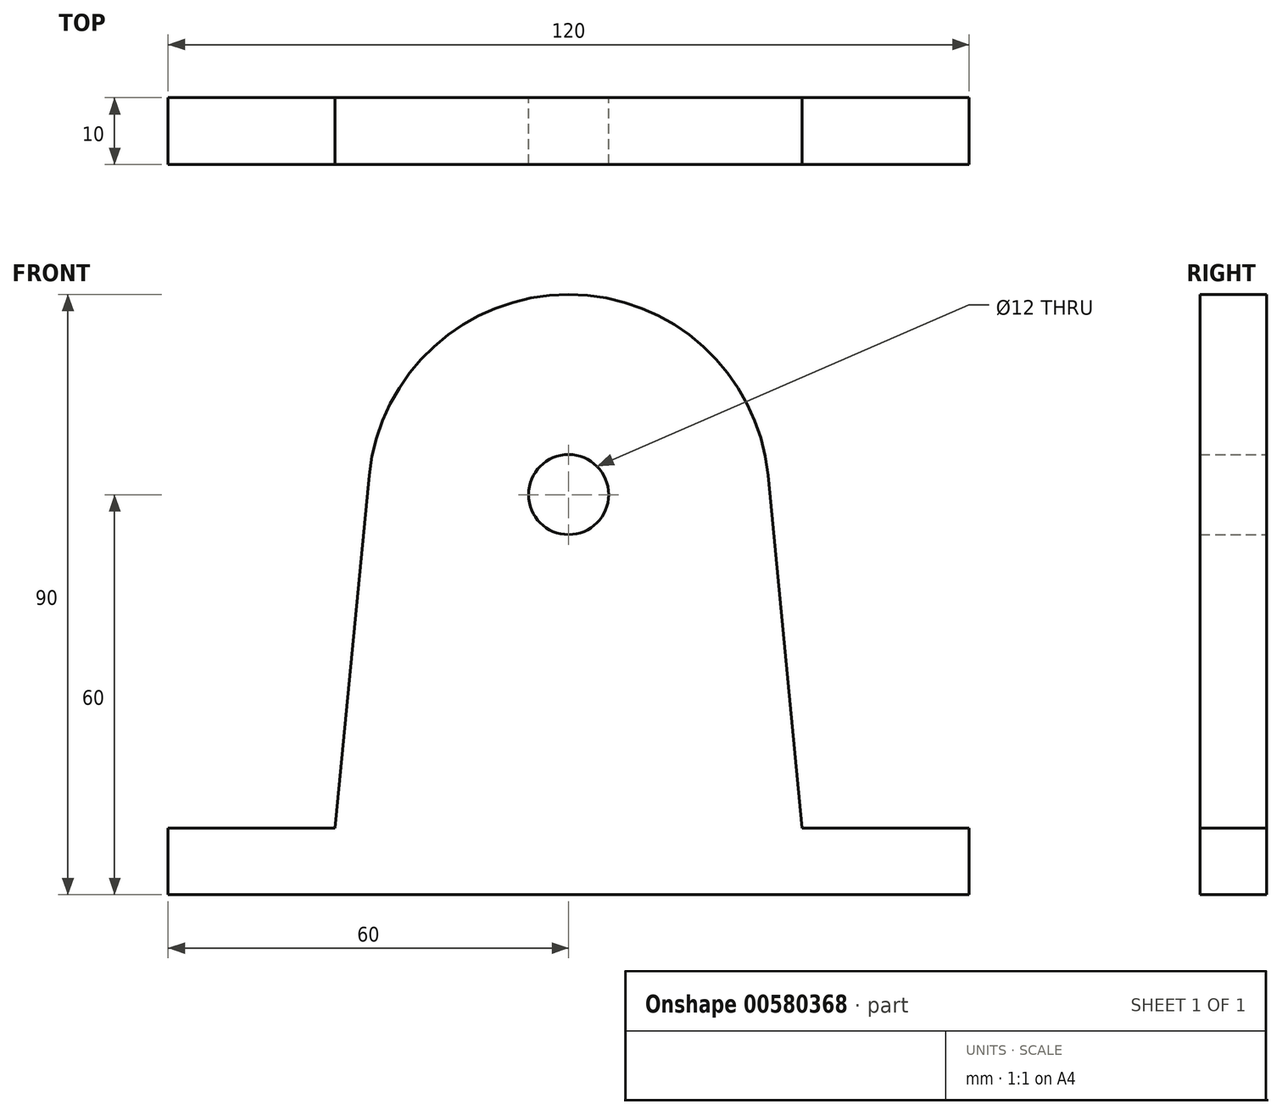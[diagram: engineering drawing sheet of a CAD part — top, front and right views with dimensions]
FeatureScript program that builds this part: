
annotation { "Feature Type Name" : "Feature", "Feature Type Description" : "" }
export const myFeature = defineFeature(function(context is Context, id is Id, definition is map)
    precondition{}
    {
        {
            var Q0;
            Q0=qCreatedBy(makeId("Front.planeOp"),FACE);
            var sketch = newSketch(context, id + "F0", { "sketchPlane" : qUnion([Q0])});
            skLineSegment(sketch, "E0", {"start": v(0, 0) * mm, "end": v(0, 50) * mm, "construction": true});
            skArc(sketch, "E1", {"start": v(29.86, 52.9) * mm, "mid": v(0, 80) * mm, "end": v(-29.86, 52.9) * mm});
            skLineSegment(sketch, "E2", {"start": v(-35, 0) * mm, "end": v(-29.86, 52.9) * mm});
            skLineSegment(sketch, "E3.MirrorCS", {"start": v(35, 0) * mm, "end": v(29.86, 52.9) * mm});
            skCircle(sketch, "E4", {"center": v(0, 50) * mm, "radius": 6 * mm});
            skPoint(sketch, "E5.middle", {"position": v(0, 0) * mm});
            skLineSegment(sketch, "E6.bottom", {"start": v(-60, 0) * mm, "end": v(-35, 0) * mm});
            skLineSegment(sketch, "E6.top", {"start": v(-60, -10) * mm, "end": v(60, -10) * mm});
            skLineSegment(sketch, "E6.left", {"start": v(-60, 0) * mm, "end": v(-60, -10) * mm});
            skLineSegment(sketch, "E6.right", {"start": v(60, 0) * mm, "end": v(60, -10) * mm});
            skLineSegment(sketch, "E7.trimOffspring", {"start": v(35, 0) * mm, "end": v(60, 0) * mm});
            skPoint(sketch, "E8.MirrorCS.end.orphan", {"position": v(35, 0) * mm});
            skSolve(sketch);
        }
        {
            var Q0;
            Q0=makeQuery(id+"F0.imprint","IMPRINT",FACE,{"disambiguationData":[TD([[makeQuery(id+"F0.imprint","IMPRINT",EDGE,{"derivedFrom":sQuery(id+"F0.wireOp",EDGE,"E1")}),1.0]])]});
            extrude(context, id + "F1", {"entities" : qUnion([Q0]), "depth" : 10 * mm, "offsetDistance" : 25 * mm});
        }
    });
